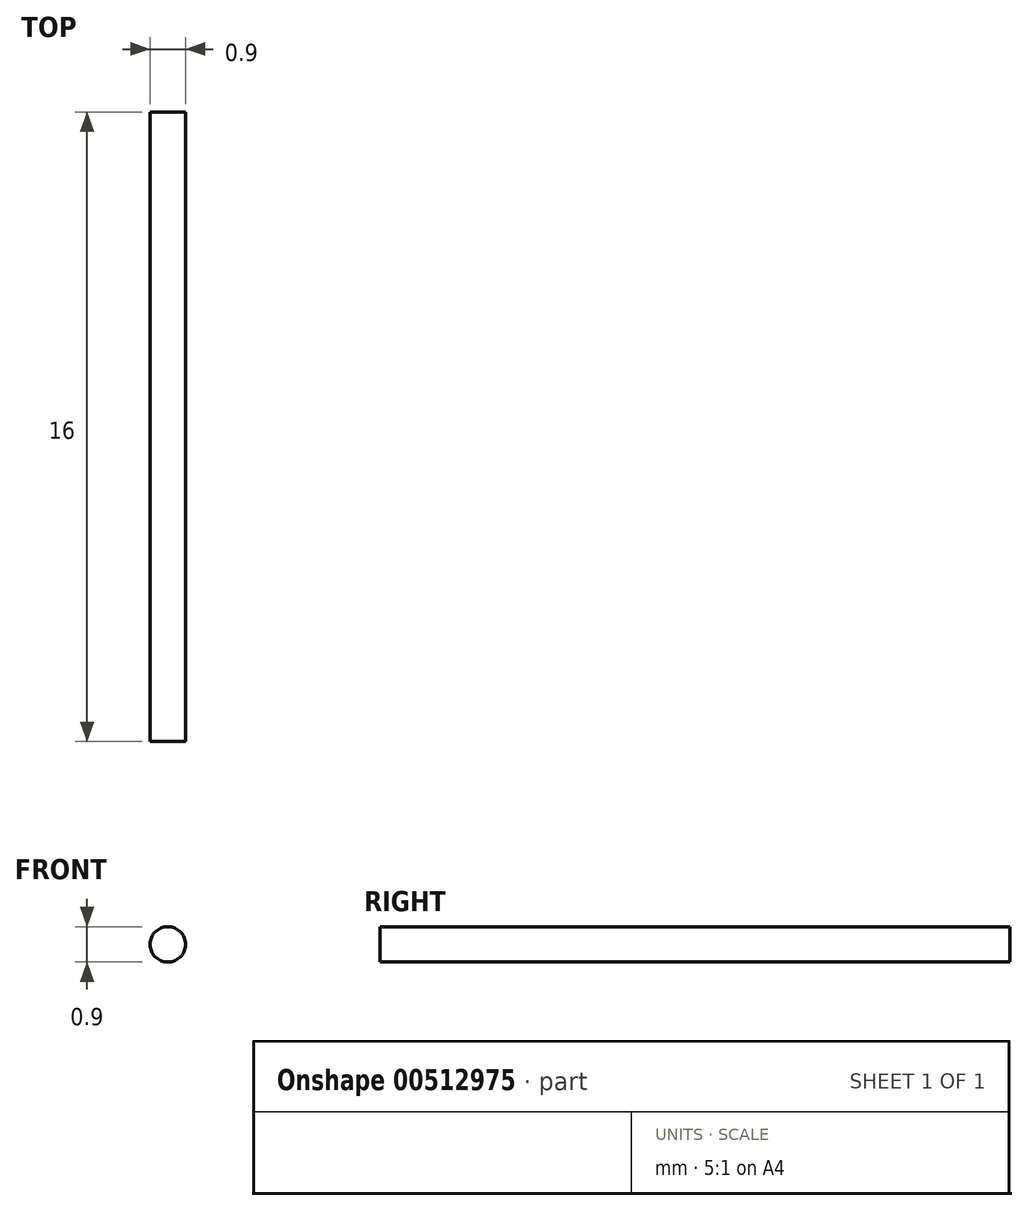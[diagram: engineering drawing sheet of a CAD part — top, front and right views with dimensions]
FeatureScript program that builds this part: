
annotation { "Feature Type Name" : "Feature", "Feature Type Description" : "" }
export const myFeature = defineFeature(function(context is Context, id is Id, definition is map)
    precondition{}
    {
        {
            var Q0;
            Q0=qCreatedBy(makeId("Front.planeOp"),FACE);
            var sketch = newSketch(context, id + "F0", { "sketchPlane" : qUnion([Q0])});
            skCircle(sketch, "E0", {"center": v(-3.36, 4.48) * mm, "radius": 0.45 * mm});
            skSolve(sketch);
        }
        {
            var Q0;
            Q0 = qSketchRegion(id + "F0", true);
            extrude(context, id + "F1", {"entities" : qUnion([Q0]), "depth" : 16 * mm, "offsetDistance" : 25 * mm});
        }
    });
